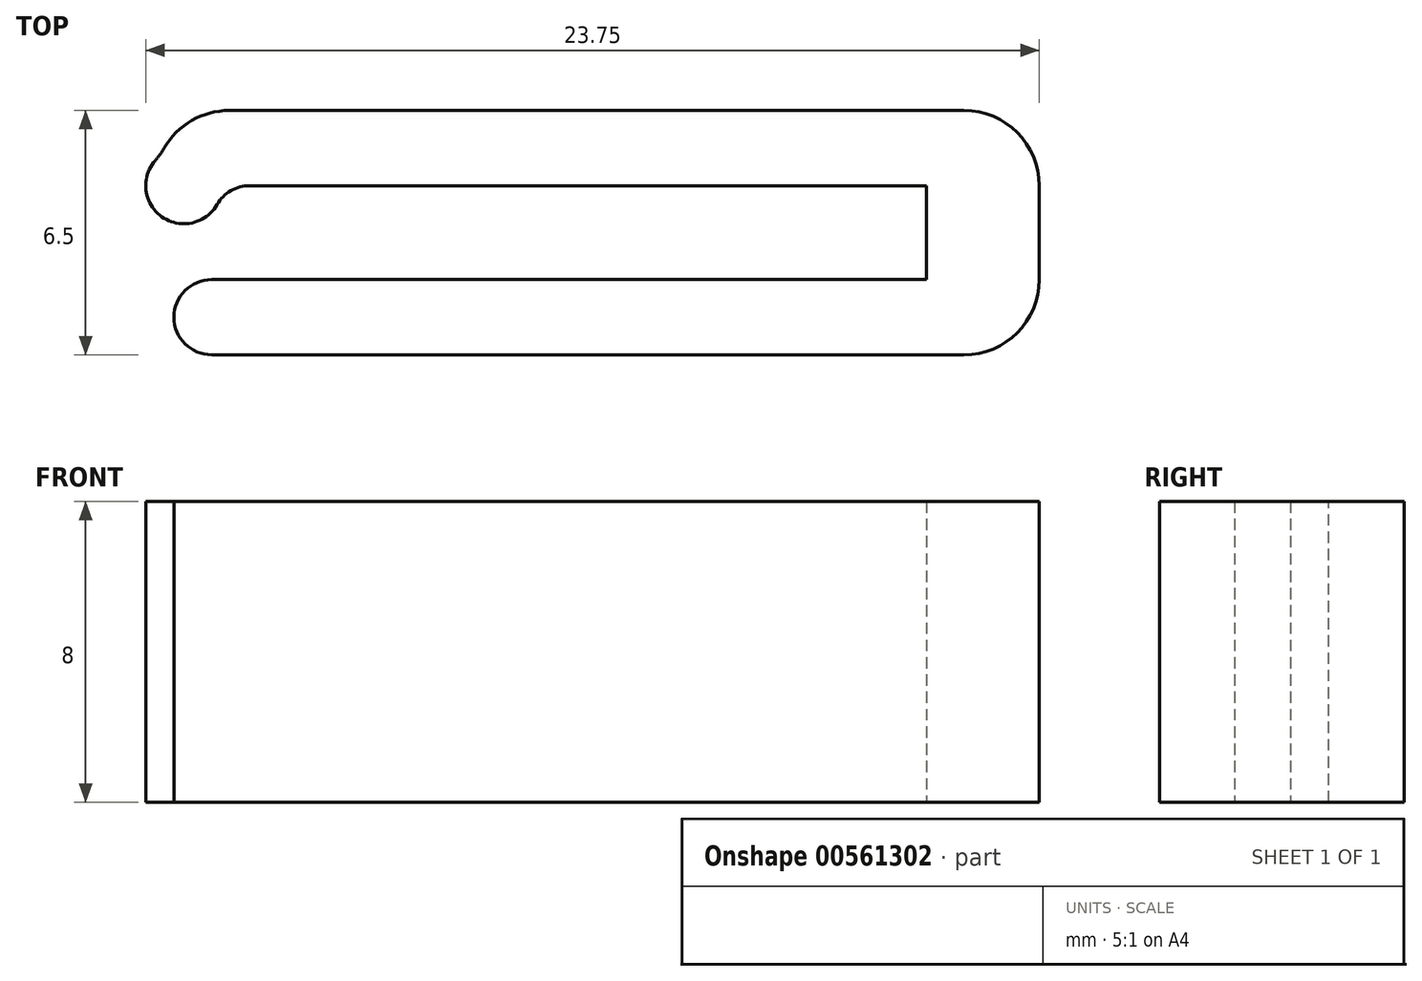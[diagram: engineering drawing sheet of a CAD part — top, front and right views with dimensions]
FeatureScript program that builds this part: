
annotation { "Feature Type Name" : "Feature", "Feature Type Description" : "" }
export const myFeature = defineFeature(function(context is Context, id is Id, definition is map)
    precondition{}
    {
        {
            var Q0;
            Q0=qCreatedBy(makeId("Top.planeOp"),FACE);
            var sketch = newSketch(context, id + "F0", { "sketchPlane" : qUnion([Q0])});
            skLineSegment(sketch, "E0.bottom", {"start": v(0, 0) * mm, "end": v(20, 0) * mm});
            skLineSegment(sketch, "E0.right", {"start": v(20, 0) * mm, "end": v(20, 2.5) * mm});
            skLineSegment(sketch, "E1.bottom", {"start": v(0, -2) * mm, "end": v(23, -2) * mm});
            skLineSegment(sketch, "E1.top", {"start": v(0, 4.5) * mm, "end": v(23, 4.5) * mm});
            skLineSegment(sketch, "E1.left", {"start": v(0, -2) * mm, "end": v(0, 0) * mm});
            skLineSegment(sketch, "E1.right", {"start": v(23, -2) * mm, "end": v(23, 4.5) * mm});
            skLineSegment(sketch, "E2.trimOffspring", {"start": v(0, 3.48) * mm, "end": v(0, 4.5) * mm});
            skArc(sketch, "E3", {"start": v(0, 3.48) * mm, "mid": v(-0.35, 1.7) * mm, "end": v(1.28, 2.5) * mm});
            skLineSegment(sketch, "E4.trimOffspring", {"start": v(1.28, 2.5) * mm, "end": v(20, 2.5) * mm});
            skSolve(sketch);
        }
        {
            var Q0;
            Q0 = qSketchRegion(id + "F0", true);
            extrude(context, id + "F1", {"entities" : qUnion([Q0]), "depth" : 8 * mm, "offsetDistance" : 25 * mm});
        }
        {
            var Q0;
            Q0=makeQuery(id+"F1.opExtrude","SWEPT_EDGE",EDGE,{"disambiguationData":[OSD([sQuery(id+"F0.wireOp",EDGE,"E1.bottom"),sQuery(id+"F0.wireOp",EDGE,"E1.right")])]});
            var Q1;
            Q1=makeQuery(id+"F1.opExtrude","SWEPT_EDGE",EDGE,{"disambiguationData":[OSD([sQuery(id+"F0.wireOp",EDGE,"E1.top"),sQuery(id+"F0.wireOp",EDGE,"E1.right")])]});
            var Q2;
            Q2=makeQuery(id+"F1.opExtrude","SWEPT_EDGE",EDGE,{"disambiguationData":[OSD([sQuery(id+"F0.wireOp",EDGE,"E2.trimOffspring"),sQuery(id+"F0.wireOp",EDGE,"E3")])]});
            fillet(context, id + "F2", {"entities" : qUnion([Q0, Q1, Q2]), "radius" : 2 * mm, "tangentPropagation" : true, "allowEdgeOverflow" : false});
        }
        {
            var Q0;
            Q0=makeQuery(id+"F1.opExtrude","SWEPT_EDGE",EDGE,{"disambiguationData":[OSD([sQuery(id+"F0.wireOp",EDGE,"E3"),sQuery(id+"F0.wireOp",EDGE,"E4.trimOffspring")])]});
            fillet(context, id + "F3", {"entities" : qUnion([Q0]), "radius" : 1 * mm, "tangentPropagation" : true, "allowEdgeOverflow" : false});
        }
        {
            var Q0;
            Q0=makeQuery(id+"F1.opExtrude","SWEPT_EDGE",EDGE,{"disambiguationData":[OSD([sQuery(id+"F0.wireOp",EDGE,"E1.top"),sQuery(id+"F0.wireOp",EDGE,"E2.trimOffspring")])]});
            fillet(context, id + "F4", {"entities" : qUnion([Q0]), "radius" : 2 * mm, "tangentPropagation" : true, "allowEdgeOverflow" : false});
        }
        {
            var Q0;
            Q0=makeQuery(id+"F1.opExtrude","SWEPT_EDGE",EDGE,{"disambiguationData":[OSD([sQuery(id+"F0.wireOp",EDGE,"E0.bottom"),sQuery(id+"F0.wireOp",EDGE,"E1.left")])]});
            var Q1;
            Q1=makeQuery(id+"F1.opExtrude","SWEPT_EDGE",EDGE,{"disambiguationData":[OSD([sQuery(id+"F0.wireOp",EDGE,"E1.bottom"),sQuery(id+"F0.wireOp",EDGE,"E1.left")])]});
            fillet(context, id + "F5", {"entities" : qUnion([Q0, Q1]), "radius" : 1 * mm, "tangentPropagation" : true, "allowEdgeOverflow" : false});
        }
    });
